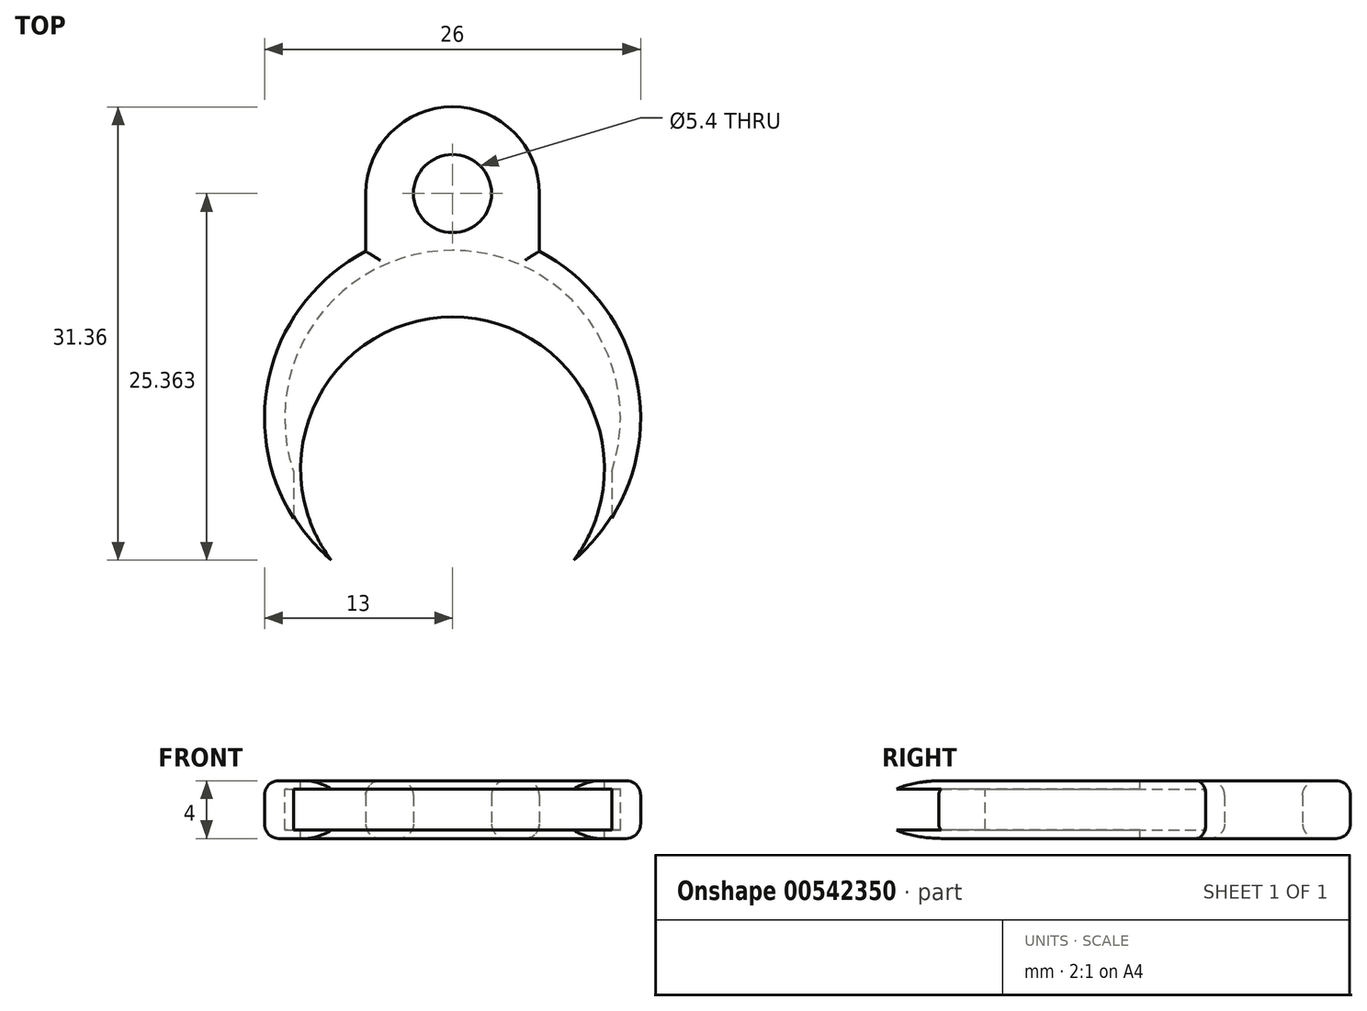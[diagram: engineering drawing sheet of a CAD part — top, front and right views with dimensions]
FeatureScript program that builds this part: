
annotation { "Feature Type Name" : "Feature", "Feature Type Description" : "" }
export const myFeature = defineFeature(function(context is Context, id is Id, definition is map)
    precondition{}
    {
        {
            var Q0;
            Q0=qCreatedBy(makeId("Top.planeOp"),FACE);
            var sketch = newSketch(context, id + "F0", { "sketchPlane" : qUnion([Q0])});
            skCircle(sketch, "E0", {"center": v(0, 0) * mm, "radius": 13 * mm});
            skLineSegment(sketch, "E1.bottom", {"start": v(-6, 11.53) * mm, "end": v(6, 11.53) * mm});
            skLineSegment(sketch, "E1.top", {"start": v(-6, 21.53) * mm, "end": v(6, 21.53) * mm});
            skLineSegment(sketch, "E1.left", {"start": v(-6, 11.53) * mm, "end": v(-6, 21.53) * mm});
            skLineSegment(sketch, "E1.right", {"start": v(6, 11.53) * mm, "end": v(6, 21.53) * mm});
            skCircle(sketch, "E2", {"center": v(0, 15.53) * mm, "radius": 2.7 * mm});
            skPoint(sketch, "E2.centerSnap0", {"position": v(0, 21.53) * mm});
            skSolve(sketch);
        }
        {
            var Q0;
            Q0 = qSketchRegion(id + "F0", true);
            extrude(context, id + "F1", {"entities" : qUnion([Q0]), "endBound" : BoundingType.SYMMETRIC, "depth" : 4 * mm, "offsetDistance" : 25 * mm});
        }
        {
            var Q0;
            Q0=makeQuery(id+"F1.opExtrude","SWEPT_EDGE",EDGE,{"disambiguationData":[OSD([sQuery(id+"F0.wireOp",EDGE,"E1.top"),sQuery(id+"F0.wireOp",EDGE,"E1.left")])]});
            var Q1;
            Q1=makeQuery(id+"F1.opExtrude","SWEPT_EDGE",EDGE,{"disambiguationData":[OSD([sQuery(id+"F0.wireOp",EDGE,"E1.top"),sQuery(id+"F0.wireOp",EDGE,"E1.right")])]});
            fillet(context, id + "F2", {"entities" : qUnion([Q0, Q1]), "radius" : 6 * mm, "tangentPropagation" : true, "allowEdgeOverflow" : false});
        }
        {
            var Q0;
            Q0=makeQuery(id+"F1.opExtrude","CAP_EDGE",EDGE,{"disambiguationData":[OSD([sQuery(id+"F0.wireOp",EDGE,"E0")])],"isStart":false});
            var Q1;
            Q1=makeQuery(id+"F1.opExtrude","CAP_EDGE",EDGE,{"disambiguationData":[OSD([sQuery(id+"F0.wireOp",EDGE,"E0")])],"isStart":true});
            fillet(context, id + "F3", {"entities" : qUnion([Q0, Q1]), "radius" : 1 * mm, "tangentPropagation" : true, "allowEdgeOverflow" : false});
        }
        {
            var Q0;
            Q0=makeQuery(id+"F1.opExtrude","CAP_EDGE",EDGE,{"disambiguationData":[OSD([sQuery(id+"F0.wireOp",EDGE,"E1.left")])],"isStart":false});
            var Q1;
            Q1=makeQuery(id+"F1.opExtrude","CAP_EDGE",EDGE,{"disambiguationData":[OSD([sQuery(id+"F0.wireOp",EDGE,"E1.right")])],"isStart":false});
            fillet(context, id + "F4", {"entities" : qUnion([Q0, Q1]), "radius" : 1 * mm, "tangentPropagation" : true, "allowEdgeOverflow" : false});
        }
        {
            var Q0;
            Q0=makeQuery(id+"F1.opExtrude","CAP_EDGE",EDGE,{"disambiguationData":[OSD([sQuery(id+"F0.wireOp",EDGE,"E1.right")])],"isStart":true});
            var Q1;
            Q1=makeQuery(id+"F1.opExtrude","CAP_EDGE",EDGE,{"disambiguationData":[OSD([sQuery(id+"F0.wireOp",EDGE,"E1.left")])],"isStart":true});
            fillet(context, id + "F5", {"entities" : qUnion([Q0, Q1]), "radius" : 1 * mm, "tangentPropagation" : true, "allowEdgeOverflow" : false});
        }
        {
            var Q0;
            Q0=makeQuery(id+"F1.opExtrude","CAP_EDGE",EDGE,{"disambiguationData":[OSD([sQuery(id+"F0.wireOp",EDGE,"E2")])],"isStart":false});
            fillet(context, id + "F6", {"entities" : qUnion([Q0]), "radius" : 1 * mm, "tangentPropagation" : true, "allowEdgeOverflow" : false});
        }
        {
            var Q0;
            Q0=makeQuery(id+"F1.opExtrude","CAP_EDGE",EDGE,{"disambiguationData":[OSD([sQuery(id+"F0.wireOp",EDGE,"E2")])],"isStart":true});
            fillet(context, id + "F7", {"entities" : qUnion([Q0]), "radius" : 1 * mm, "tangentPropagation" : true, "allowEdgeOverflow" : false});
        }
        {
            var Q0;
            Q0=makeQuery(id+"F1.opExtrude","CAP_FACE",FACE,{"disambiguationData":[OSD([sQuery(id+"F0.wireOp",EDGE,"E0"),sQuery(id+"F0.wireOp",EDGE,"E1.top"),sQuery(id+"F0.wireOp",EDGE,"E1.left"),sQuery(id+"F0.wireOp",EDGE,"E1.right"),sQuery(id+"F0.wireOp",EDGE,"E2")])],"isStart":false});
            var sketch = newSketch(context, id + "F8", { "sketchPlane" : qUnion([Q0])});
            skCircle(sketch, "E3", {"center": v(0, -3.5) * mm, "radius": 10.5 * mm});
            skSolve(sketch);
        }
        {
            var Q0;
            Q0 = qSketchRegion(id + "F8", true);
            extrude(context, id + "F9", {"entities" : qUnion([Q0]), "operationType" : NewBodyOperationType.REMOVE, "endBound" : BoundingType.THROUGH_ALL, "oppositeDirection" : true, "depth" : 25 * mm, "offsetDistance" : 25 * mm});
        }
        {
            var Q0;
            Q0=qCreatedBy(makeId("Top.planeOp"),FACE);
            var sketch = newSketch(context, id + "F10", { "sketchPlane" : qUnion([Q0])});
            skCircle(sketch, "E4", {"center": v(0, 0) * mm, "radius": 11.6 * mm});
            skLineSegment(sketch, "E5.bottom", {"start": v(-11, -3.7) * mm, "end": v(11, -3.7) * mm});
            skLineSegment(sketch, "E5.top", {"start": v(-11, -15.96) * mm, "end": v(11, -15.96) * mm});
            skLineSegment(sketch, "E5.left", {"start": v(-11, -3.7) * mm, "end": v(-11, -15.96) * mm});
            skLineSegment(sketch, "E5.right", {"start": v(11, -3.7) * mm, "end": v(11, -15.96) * mm});
            skSolve(sketch);
        }
        {
            var Q0;
            Q0 = qSketchRegion(id + "F10", true);
            extrude(context, id + "F11", {"entities" : qUnion([Q0]), "operationType" : NewBodyOperationType.REMOVE, "endBound" : BoundingType.SYMMETRIC, "oppositeDirection" : true, "depth" : 2.8 * mm, "offsetDistance" : 25 * mm});
        }
    });
